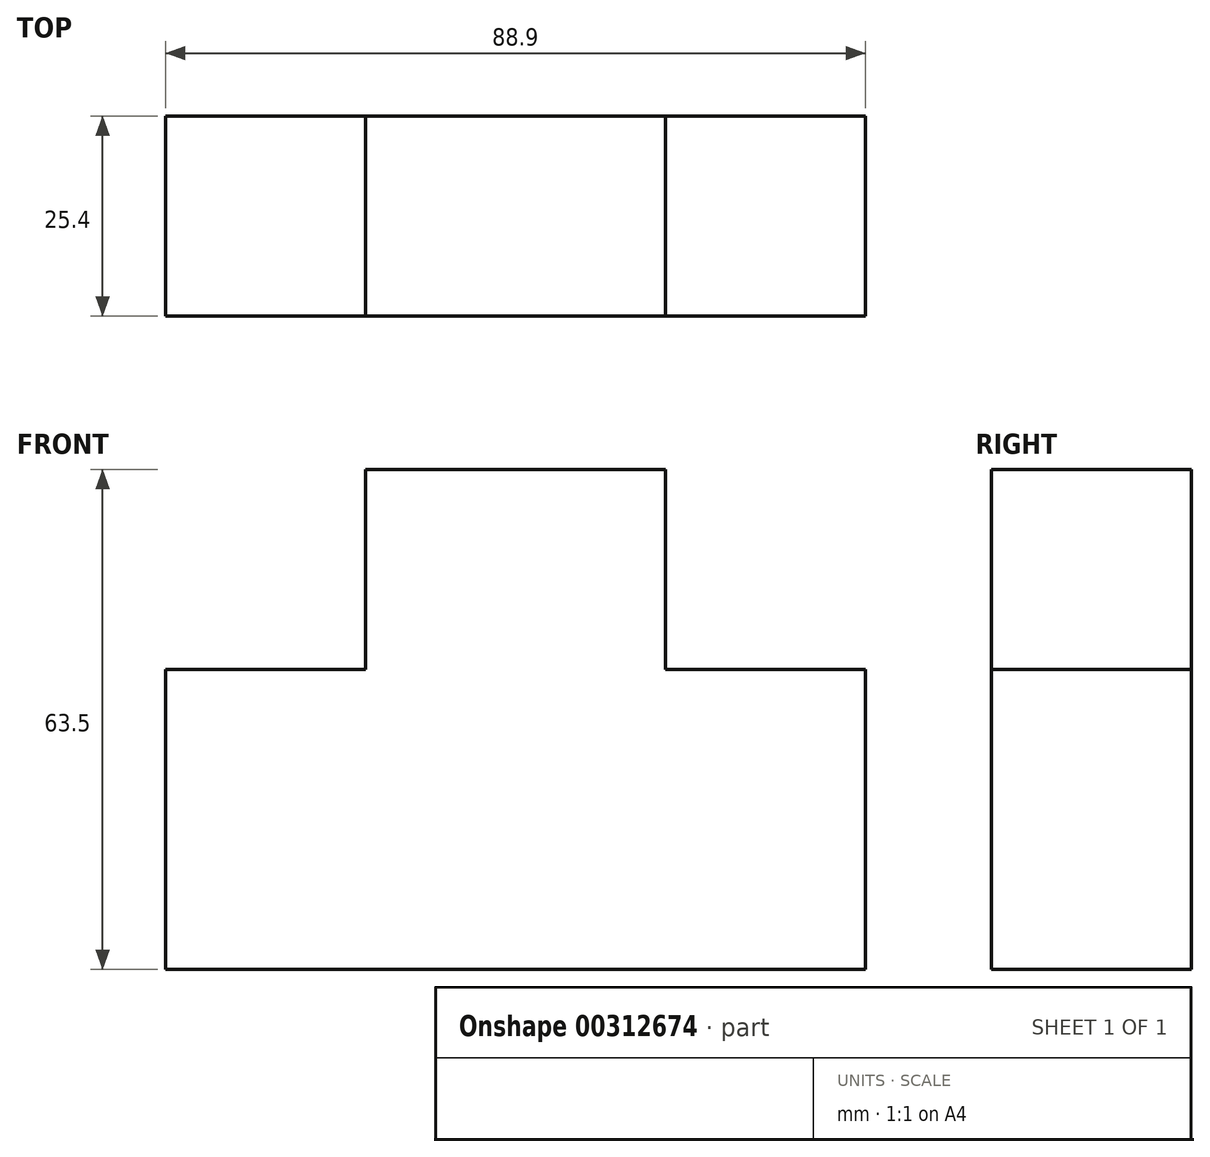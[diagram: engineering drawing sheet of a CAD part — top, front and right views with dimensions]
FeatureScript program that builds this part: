
annotation { "Feature Type Name" : "Feature", "Feature Type Description" : "" }
export const myFeature = defineFeature(function(context is Context, id is Id, definition is map)
    precondition{}
    {
        {
            var Q0;
            Q0=qCreatedBy(makeId("Front.planeOp"),FACE);
            var sketch = newSketch(context, id + "F0", { "sketchPlane" : qUnion([Q0])});
            skLineSegment(sketch, "E0", {"start": v(-61.02, -15.45) * mm, "end": v(-61.02, -53.55) * mm});
            skLineSegment(sketch, "E1", {"start": v(-61.02, -53.55) * mm, "end": v(27.88, -53.55) * mm});
            skLineSegment(sketch, "E2", {"start": v(27.88, -53.55) * mm, "end": v(27.88, -15.45) * mm});
            skLineSegment(sketch, "E3", {"start": v(27.88, -15.45) * mm, "end": v(2.48, -15.45) * mm});
            skLineSegment(sketch, "E4", {"start": v(2.48, -15.45) * mm, "end": v(2.48, 9.95) * mm});
            skLineSegment(sketch, "E5", {"start": v(2.48, 9.95) * mm, "end": v(-35.62, 9.95) * mm});
            skLineSegment(sketch, "E6", {"start": v(-35.62, 9.95) * mm, "end": v(-35.62, -15.45) * mm});
            skLineSegment(sketch, "E7", {"start": v(-35.62, -15.45) * mm, "end": v(-61.02, -15.45) * mm});
            skSolve(sketch);
        }
        {
            var Q0;
            Q0 = qSketchRegion(id + "F0", true);
            var Q1;
            Q1=makeQuery(id+"F0.imprint","IMPRINT",FACE,{"disambiguationData":[TD([[makeQuery(id+"F0.imprint","IMPRINT",EDGE,{"derivedFrom":sQuery(id+"F0.wireOp",EDGE,"E0")}),1.0]])]});
            extrude(context, id + "F1", {"entities" : qUnion([Q0, Q1]), "depth" : 25.4 * mm});
        }
    });
